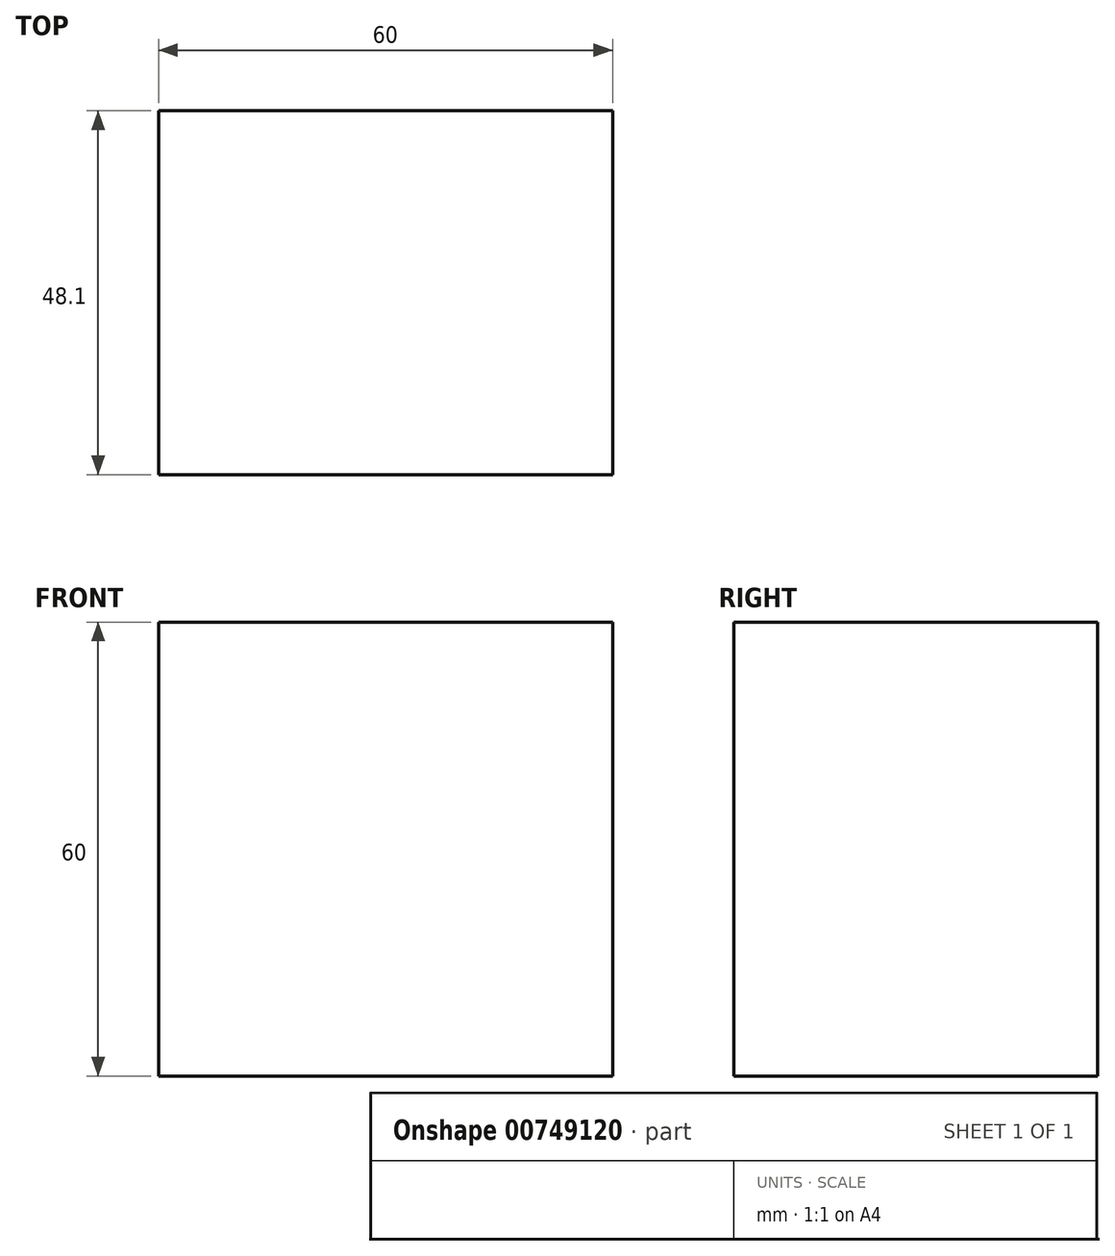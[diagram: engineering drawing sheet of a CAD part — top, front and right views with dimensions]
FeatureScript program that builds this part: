
annotation { "Feature Type Name" : "Feature", "Feature Type Description" : "" }
export const myFeature = defineFeature(function(context is Context, id is Id, definition is map)
    precondition{}
    {
        {
            var Q0;
            Q0=qCreatedBy(makeId("Front.planeOp"),FACE);
            var sketch = newSketch(context, id + "F0", { "sketchPlane" : qUnion([Q0])});
            skLineSegment(sketch, "E0", {"start": v(-36.5, 38.28) * mm, "end": v(-36.5, -21.72) * mm});
            skLineSegment(sketch, "E1", {"start": v(-36.5, -21.72) * mm, "end": v(23.5, -21.72) * mm});
            skLineSegment(sketch, "E2", {"start": v(23.5, -21.72) * mm, "end": v(23.5, 38.28) * mm});
            skLineSegment(sketch, "E3", {"start": v(23.5, 38.28) * mm, "end": v(-36.5, 38.28) * mm});
            skSolve(sketch);
        }
        {
            var Q0;
            Q0=makeQuery(id+"F0.imprint","IMPRINT",FACE,{"disambiguationData":[TD([[makeQuery(id+"F0.imprint","IMPRINT",EDGE,{"derivedFrom":sQuery(id+"F0.wireOp",EDGE,"E0")}),1.0]])]});
            extrude(context, id + "F1", {"entities" : qUnion([Q0]), "depth" : 48.1 * mm, "offsetDistance" : 25 * mm});
        }
    });
